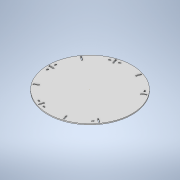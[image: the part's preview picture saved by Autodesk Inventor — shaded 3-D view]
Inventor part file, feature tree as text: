
AUTODESK INVENTOR PART (.ipt)
format: ipt  version: 2020 (Build 240168000, 168)  size: 376,320 bytes
history: native  units: mm
features: extrude x2, sketch x1, projected_geometry x1
ambient origin geometry x8: Origin, YZ Plane, XZ Plane, XY Plane, X Axis, Y Axis, Z Axis, Center Point
bodies: Solid1 (feature_tree)
feature tree (4):
  extrude  "Extrusion1"  Depth=7.5mm
  extrude  "Extrusion2"  Depth=7.5mm
  sketch  "Sketch1"  dims[d3=7.5mm d6=30.0mm d7=3.5mm d8=3.5mm d12=7.0mm d13=0.0mm d14=7.5mm d16=13.0mm d17=13.0mm d18=13.5mm d19=1.75mm d20=20.0mm d24=0.0mm d25=0.0mm d26=8.25mm d27=33.5mm d28=7.5mm d36=600.0mm]
  projected_geometry  "Projected Loop1"
